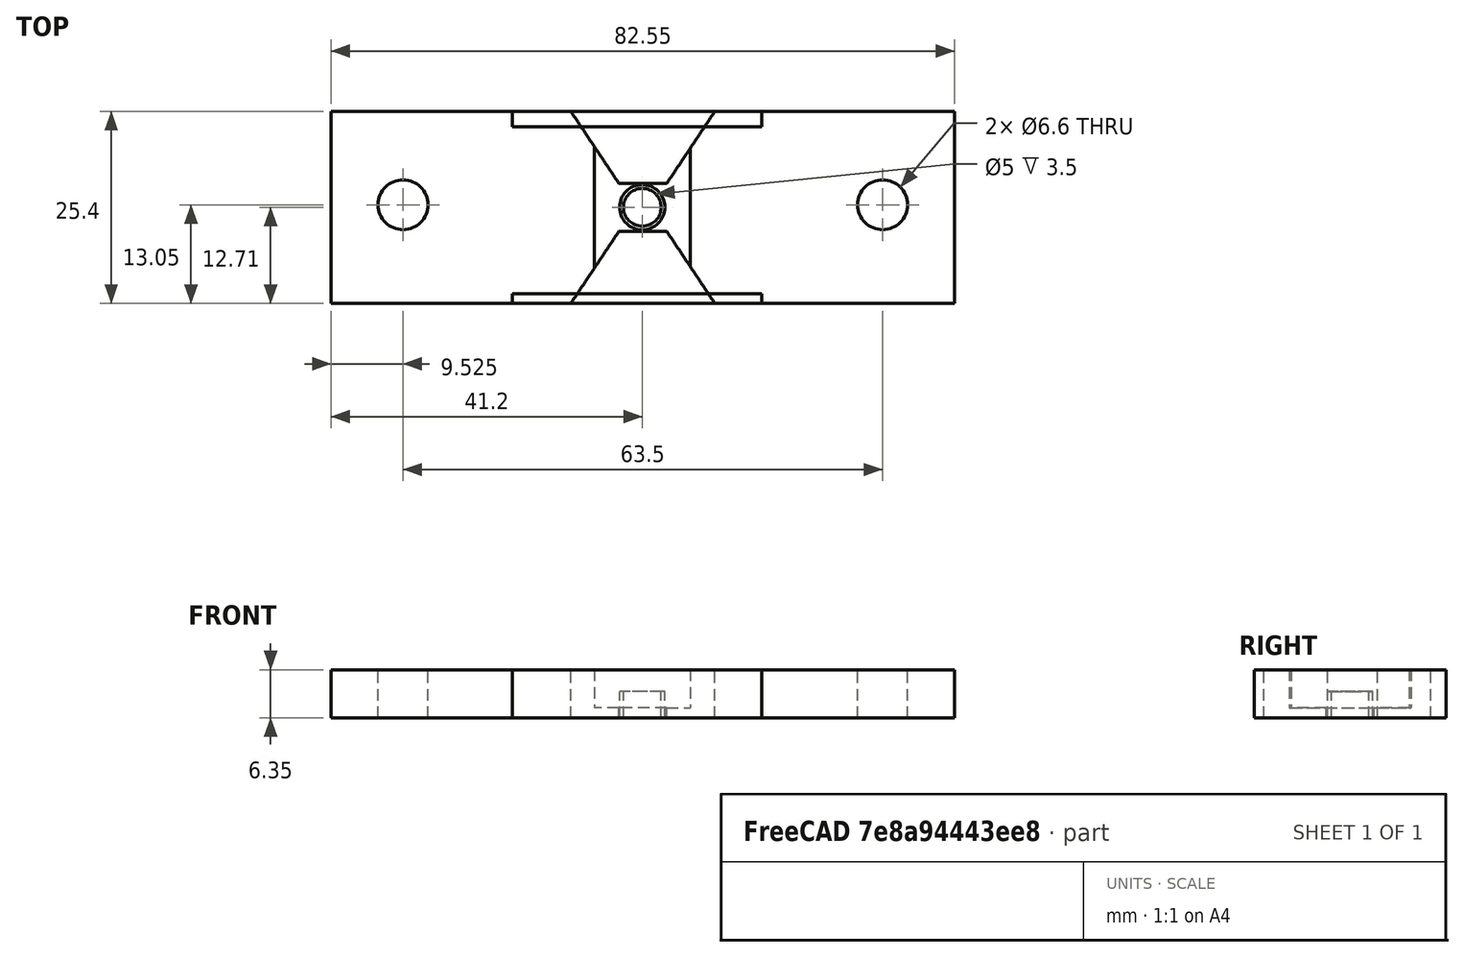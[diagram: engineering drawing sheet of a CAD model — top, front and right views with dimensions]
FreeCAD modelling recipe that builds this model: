
FCSTD DOCUMENT  (FreeCAD 0.16R6707 (Git))
Label: graphite3
License: All rights reserved
LicenseURL: http://en.wikipedia.org/wiki/All_rights_reserved
objects: Part::Cylinder×4, Part::Box×3, Part::Cut×2, Part::MultiFuse×1, Part::Feature×1, Part::Extrusion×1
note: 12 computed .brp shape members not serialized (recipe doc carries the construction recipe); baked Part::Feature solids carry a one-line shape summary decoded from their .brp

FEATURE [Part::Cylinder] Cylinder  label="Hole1"
  Angle = 360
  Height = 10
  Placement = pos=(9.525,-12.7,0) rot=(0,0,1;0rad)
  Radius = 3.302
FEATURE [Part::Cylinder] Cylinder001  label="Hole2"
  Angle = 360
  Height = 10
  Placement = pos=(73.025,-12.7,0) rot=(0,0,1;0rad)
  Radius = 3.302
FEATURE [Part::Box] Box  label="Support1"
  Height = 6.35
  Length = 33
  Placement = pos=(24,-2.35,0) rot=(0,0,1;0rad)
  Width = 2
FEATURE [Part::Box] Box001  label="Support2"
  Height = 6.35
  Length = 33
  Placement = pos=(24,-25.753,0) rot=(0,0,1;0rad)
  Width = 1.25
FEATURE [Part::Box] Box002  label="Thinner"
  Height = 17
  Length = 12.7
  Placement = pos=(34.85,-21.35,1.35) rot=(0,0,1;0rad)
  Width = 16.7
FEATURE [Part::MultiFuse] Fusion
  Shapes = -> [Cylinder,Cylinder001,Box002]
FEATURE [Part::Feature] rect3338
  shape: bbox 82.55 x 25.4 x 2e-07 mm, 0 faces, 0 solids (baked)
FEATURE [Part::Extrusion] Extrude
  Base = -> rect3338
  Dir = (0,0,6.35)
  Solid = true
FEATURE [Part::Cut] Cut
  Base = -> Extrude
  Tool = -> Fusion
FEATURE [Part::Cylinder] Cylinder002  label="Cylinder"
  Angle = 360
  Height = 3.5
  Placement = pos=(41.2,-13.04,0) rot=(0,0,1;0rad)
  Radius = 3
FEATURE [Part::Cylinder] Cylinder003  label="Cylinder001"
  Angle = 360
  Height = 16
  Placement = pos=(41.2,-13.04,0) rot=(0,0,1;0rad)
  Radius = 2.5
FEATURE [Part::Cut] Cut001
  Base = -> Cylinder002
  Tool = -> Cylinder003
